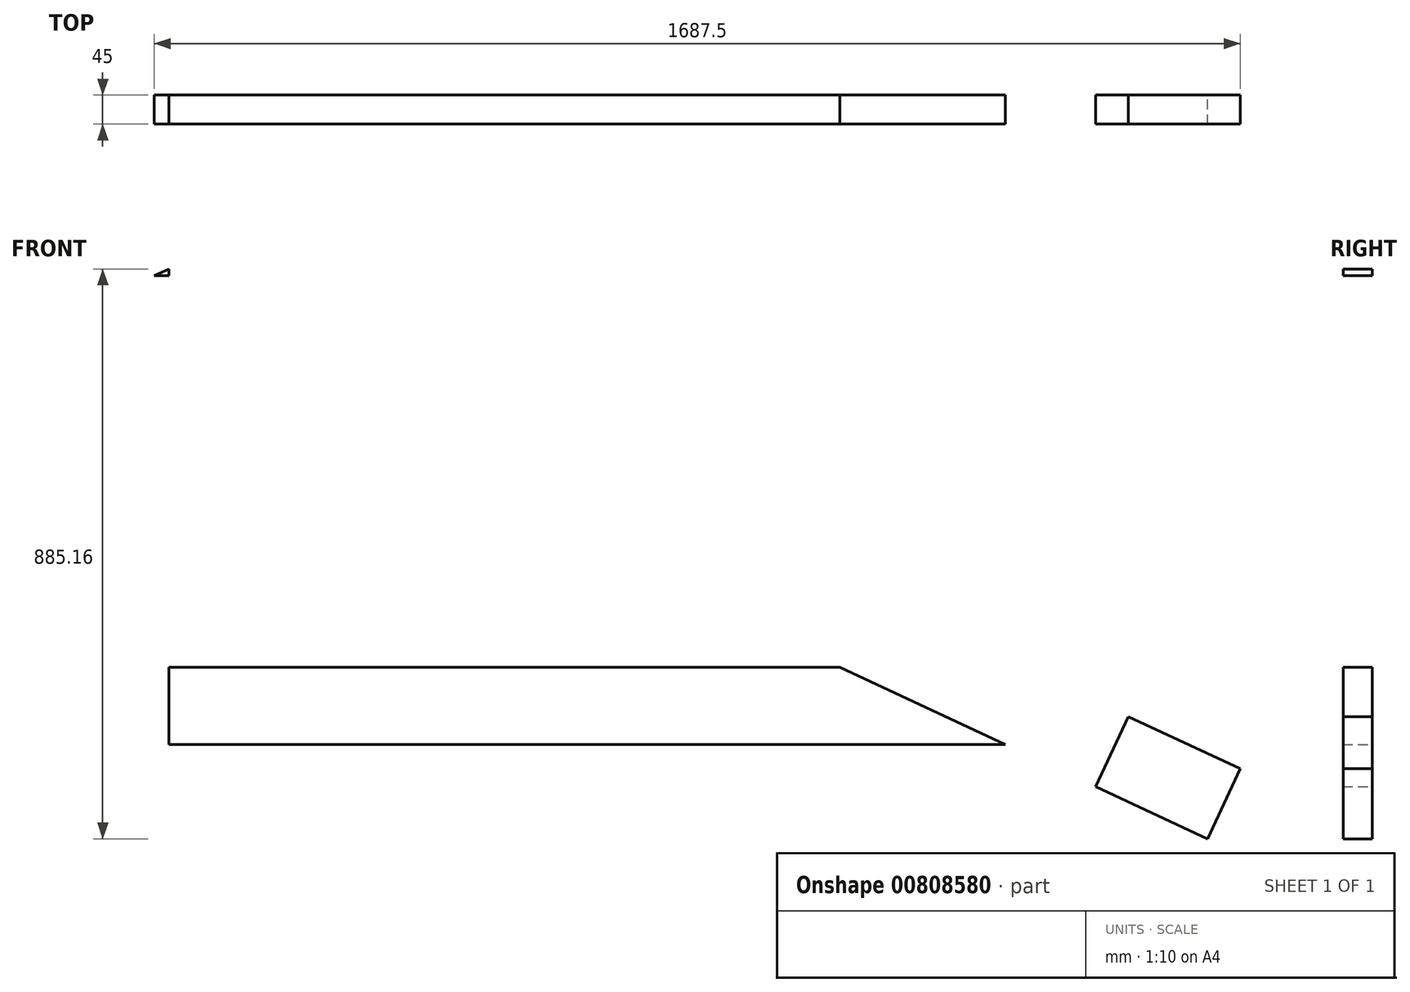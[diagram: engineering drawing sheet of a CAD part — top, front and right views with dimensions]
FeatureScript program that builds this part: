
annotation { "Feature Type Name" : "Feature", "Feature Type Description" : "" }
export const myFeature = defineFeature(function(context is Context, id is Id, definition is map)
    precondition{}
    {
        {
            var Q0;
            Q0=qCreatedBy(makeId("Front.planeOp"),FACE);
            var sketch = newSketch(context, id + "F0", { "sketchPlane" : qUnion([Q0])});
            skLineSegment(sketch, "E0", {"start": v(1614.29, 0) * mm, "end": v(0, 752.75) * mm});
            skLineSegment(sketch, "E1", {"start": v(0, 146.55) * mm, "end": v(1300, 146.55) * mm});
            skLineSegment(sketch, "E2", {"start": v(0, 885.16) * mm, "end": v(1665, 108.76) * mm});
            skLineSegment(sketch, "E3", {"start": v(1665, 108.76) * mm, "end": v(1614.29, 0) * mm});
            skLineSegment(sketch, "E4", {"start": v(0, 752.75) * mm, "end": v(-1614.29, 0) * mm});
            skLineSegment(sketch, "E5", {"start": v(0, 885.16) * mm, "end": v(-1665, 108.76) * mm});
            skLineSegment(sketch, "E6", {"start": v(-1665, 108.76) * mm, "end": v(-1614.29, 0) * mm});
            skLineSegment(sketch, "E7", {"start": v(0, 146.55) * mm, "end": v(-1300, 146.55) * mm});
            skLineSegment(sketch, "E8", {"start": v(1300, 146.55) * mm, "end": v(1300, 1.55) * mm});
            skLineSegment(sketch, "E9", {"start": v(1300, 1.55) * mm, "end": v(1210, 1.55) * mm});
            skLineSegment(sketch, "E10", {"start": v(1210, 1.55) * mm, "end": v(1210, 146.55) * mm});
            skLineSegment(sketch, "E11", {"start": v(-1042.66, 266.55) * mm, "end": v(1042.66, 266.55) * mm});
            skLineSegment(sketch, "E12", {"start": v(0, 146.55) * mm, "end": v(0, 885.16) * mm});
            skLineSegment(sketch, "E13", {"start": v(-1300, 146.55) * mm, "end": v(-1300, 1.55) * mm});
            skLineSegment(sketch, "E14", {"start": v(-1300, 1.55) * mm, "end": v(-1210, 1.55) * mm});
            skLineSegment(sketch, "E15", {"start": v(-1210, 1.55) * mm, "end": v(-1210, 146.55) * mm});
            skLineSegment(sketch, "E16", {"start": v(1614.29, 0) * mm, "end": v(1300, 0) * mm});
            skLineSegment(sketch, "E17", {"start": v(-1614.29, 0) * mm, "end": v(-1300, 0) * mm});
            skLineSegment(sketch, "E18", {"start": v(0, 885.16) * mm, "end": v(10.57, 907.82) * mm});
            skLineSegment(sketch, "E19", {"start": v(45.9, 891.34) * mm, "end": v(62.05, 925.66) * mm});
            skLineSegment(sketch, "E20", {"start": v(62.05, 925.66) * mm, "end": v(128.24, 894.87) * mm});
            skLineSegment(sketch, "E21", {"start": v(128.24, 894.87) * mm, "end": v(112.22, 860.42) * mm});
            skLineSegment(sketch, "E22", {"start": v(378.14, 735.02) * mm, "end": v(394.16, 769.47) * mm});
            skLineSegment(sketch, "E23", {"start": v(394.16, 769.47) * mm, "end": v(460.35, 738.69) * mm});
            skLineSegment(sketch, "E24", {"start": v(460.35, 738.69) * mm, "end": v(444.33, 704.23) * mm});
            skLineSegment(sketch, "E25", {"start": v(710.33, 578.61) * mm, "end": v(726.2, 613.14) * mm});
            skLineSegment(sketch, "E26", {"start": v(726.2, 613.14) * mm, "end": v(792.4, 582.35) * mm});
            skLineSegment(sketch, "E27", {"start": v(792.4, 582.35) * mm, "end": v(776.37, 547.9) * mm});
            skLineSegment(sketch, "E28", {"start": v(1043.87, 425.98) * mm, "end": v(1059.93, 460.42) * mm});
            skLineSegment(sketch, "E29", {"start": v(1059.93, 460.42) * mm, "end": v(1126.12, 429.63) * mm});
            skLineSegment(sketch, "E30", {"start": v(1126.12, 429.63) * mm, "end": v(1110.1, 395.18) * mm});
            skLineSegment(sketch, "E31", {"start": v(1376.45, 270.81) * mm, "end": v(1392.51, 305.25) * mm});
            skLineSegment(sketch, "E32", {"start": v(1392.51, 305.25) * mm, "end": v(1458.7, 274.47) * mm});
            skLineSegment(sketch, "E33", {"start": v(1458.7, 274.47) * mm, "end": v(1442.68, 240.01) * mm});
            skLineSegment(sketch, "E34", {"start": v(1364.07, 314.8) * mm, "end": v(1376.8, 352.72) * mm});
            skLineSegment(sketch, "E35", {"start": v(1762.27, 181.23) * mm, "end": v(1774.99, 219.15) * mm});
            skLineSegment(sketch, "E36", {"start": v(1376.8, 352.72) * mm, "end": v(1774.99, 219.15) * mm});
            skLineSegment(sketch, "E37", {"start": v(1364.07, 314.8) * mm, "end": v(1762.27, 181.23) * mm});
            skLineSegment(sketch, "E38", {"start": v(-22.5, 874.67) * mm, "end": v(22.5, 874.67) * mm});
            skLineSegment(sketch, "E39", {"start": v(22.5, 874.67) * mm, "end": v(22.5, 1039.67) * mm});
            skLineSegment(sketch, "E40", {"start": v(22.5, 1039.67) * mm, "end": v(-22.5, 1039.67) * mm});
            skLineSegment(sketch, "E41", {"start": v(-22.5, 1039.67) * mm, "end": v(-22.5, 874.67) * mm});
            skLineSegment(sketch, "E42", {"start": v(1031.09, 468.68) * mm, "end": v(1429.28, 335.11) * mm});
            skLineSegment(sketch, "E43", {"start": v(1429.28, 335.11) * mm, "end": v(1442, 373.03) * mm});
            skLineSegment(sketch, "E44", {"start": v(1442, 373.03) * mm, "end": v(1043.8, 506.6) * mm});
            skLineSegment(sketch, "E45", {"start": v(1043.8, 506.6) * mm, "end": v(1031.09, 468.68) * mm});
            skLineSegment(sketch, "E46", {"start": v(1721.06, 158.95) * mm, "end": v(1861.06, 158.95) * mm});
            skArc(sketch, "E47", {"start": v(1721.06, 158.95) * mm, "mid": v(1791.06, 88.95) * mm, "end": v(1861.06, 158.95) * mm});
            skLineSegment(sketch, "E48", {"start": v(1689.9, 103.02) * mm, "end": v(1712.57, 92.45) * mm});
            skLineSegment(sketch, "E49", {"start": v(1712.57, 92.45) * mm, "end": v(1659.74, -20.84) * mm});
            skLineSegment(sketch, "E50", {"start": v(1659.74, -20.84) * mm, "end": v(1637.08, -10.27) * mm});
            skLineSegment(sketch, "E51", {"start": v(1637.08, -10.27) * mm, "end": v(1689.9, 103.02) * mm});
            skLineSegment(sketch, "E52", {"start": v(1300, -10) * mm, "end": v(1628.29, -10) * mm});
            skLineSegment(sketch, "E53", {"start": v(1628.29, -10) * mm, "end": v(1628.29, 0) * mm});
            skLineSegment(sketch, "E54", {"start": v(1628.29, 0) * mm, "end": v(1300, 0) * mm});
            skLineSegment(sketch, "E55", {"start": v(1300, 1.55) * mm, "end": v(1300, -2128.45) * mm});
            skLineSegment(sketch, "E56", {"start": v(1300, -2128.45) * mm, "end": v(1203, -2128.45) * mm});
            skLineSegment(sketch, "E57", {"start": v(1203, -2128.45) * mm, "end": v(1203, 1.55) * mm});
            skLineSegment(sketch, "E58", {"start": v(1203, 1.55) * mm, "end": v(1300, 1.55) * mm});
            skLineSegment(sketch, "E59", {"start": v(-1300, 1.55) * mm, "end": v(-1300, -2128.45) * mm});
            skLineSegment(sketch, "E60", {"start": v(-1300, -2128.45) * mm, "end": v(-1203, -2128.45) * mm});
            skLineSegment(sketch, "E61", {"start": v(-1203, -2128.45) * mm, "end": v(-1203, 1.55) * mm});
            skLineSegment(sketch, "E62", {"start": v(-1203, 1.55) * mm, "end": v(-1300, 1.55) * mm});
            skLineSegment(sketch, "E63", {"start": v(-1203, 1.55) * mm, "end": v(1210, 1.55) * mm});
            skLineSegment(sketch, "E64", {"start": v(-1203, -2128.45) * mm, "end": v(1203, -2128.45) * mm});
            skLineSegment(sketch, "E65.bottom", {"start": v(-603, -198.45) * mm, "end": v(575, -198.45) * mm});
            skLineSegment(sketch, "E65.top", {"start": v(-603, -896.45) * mm, "end": v(575, -896.45) * mm});
            skLineSegment(sketch, "E65.left", {"start": v(-603, -198.45) * mm, "end": v(-603, -896.45) * mm});
            skLineSegment(sketch, "E65.right", {"start": v(575, -198.45) * mm, "end": v(575, -896.45) * mm});
            skLineSegment(sketch, "E66", {"start": v(10.57, 907.82) * mm, "end": v(1442.68, 240.01) * mm});
            skLineSegment(sketch, "E67", {"start": v(1442.68, 240.01) * mm, "end": v(1432.11, 217.35) * mm});
            skLineSegment(sketch, "E68", {"start": v(1691.06, 176.38) * mm, "end": v(1432.11, 217.35) * mm});
            skLineSegment(sketch, "E69", {"start": v(1691.06, 176.38) * mm, "end": v(1695.75, 206.01) * mm});
            skLineSegment(sketch, "E70", {"start": v(1695.75, 206.01) * mm, "end": v(1671.05, 209.92) * mm});
            skLineSegment(sketch, "E71", {"start": v(1671.05, 209.92) * mm, "end": v(1666.36, 180.29) * mm});
            skLineSegment(sketch, "E72", {"start": v(1691.06, 176.38) * mm, "end": v(1688.24, 158.6) * mm});
            skLineSegment(sketch, "E73", {"start": v(1688.24, 158.6) * mm, "end": v(1391.93, 205.49) * mm});
            skLineSegment(sketch, "E74", {"start": v(1391.93, 205.49) * mm, "end": v(1394.74, 223.27) * mm});
            skLineSegment(sketch, "E75", {"start": v(1394.74, 223.27) * mm, "end": v(1432.11, 217.35) * mm});
            skLineSegment(sketch, "E76", {"start": v(1665, 108.76) * mm, "end": v(1688.24, 158.6) * mm});
            skLineSegment(sketch, "E77", {"start": v(1630.56, 124.82) * mm, "end": v(1649.2, 164.78) * mm});
            skLineSegment(sketch, "E78", {"start": v(1688.24, 158.6) * mm, "end": v(1710.9, 148.04) * mm});
            skLineSegment(sketch, "E79", {"start": v(1710.9, 148.04) * mm, "end": v(1658.07, 34.75) * mm});
            skLineSegment(sketch, "E80", {"start": v(1658.07, 34.75) * mm, "end": v(1635.42, 45.32) * mm});
            skLineSegment(sketch, "E81", {"start": v(1721.06, 158.95) * mm, "end": v(1764.06, 158.95) * mm});
            skLineSegment(sketch, "E82", {"start": v(1095.96, 489.1) * mm, "end": v(697.76, 622.68) * mm});
            skLineSegment(sketch, "E83", {"start": v(697.76, 622.68) * mm, "end": v(710.48, 660.6) * mm});
            skLineSegment(sketch, "E84", {"start": v(710.48, 660.6) * mm, "end": v(1108.68, 527.03) * mm});
            skLineSegment(sketch, "E85", {"start": v(1108.68, 527.03) * mm, "end": v(1095.96, 489.1) * mm});
            skLineSegment(sketch, "E86", {"start": v(762.82, 643.05) * mm, "end": v(365.79, 779.2) * mm});
            skLineSegment(sketch, "E87", {"start": v(365.79, 779.2) * mm, "end": v(378.5, 817.13) * mm});
            skLineSegment(sketch, "E88", {"start": v(762.82, 643.05) * mm, "end": v(775.8, 680.88) * mm});
            skLineSegment(sketch, "E89", {"start": v(775.8, 680.88) * mm, "end": v(378.5, 817.13) * mm});
            skLineSegment(sketch, "E90", {"start": v(430.96, 799.14) * mm, "end": v(33.68, 935.39) * mm});
            skLineSegment(sketch, "E91", {"start": v(33.68, 935.39) * mm, "end": v(46.65, 973.23) * mm});
            skLineSegment(sketch, "E92", {"start": v(430.96, 799.14) * mm, "end": v(443.94, 836.98) * mm});
            skLineSegment(sketch, "E93", {"start": v(443.94, 836.98) * mm, "end": v(46.65, 973.23) * mm});
            skLineSegment(sketch, "E94", {"start": v(0, 885.16) * mm, "end": v(0, 1039.67) * mm});
            skLineSegment(sketch, "E95", {"start": v(116, 949.44) * mm, "end": v(0, 949.44) * mm});
            skCircle(sketch, "E96", {"center": v(0, 949.44) * mm, "radius": 116 * mm});
            skCircle(sketch, "E97", {"center": v(0, 949.44) * mm, "radius": 96 * mm});
            skLineSegment(sketch, "E98", {"start": v(1491.27, 189.77) * mm, "end": v(1440.55, 81.01) * mm});
            skSolve(sketch);
        }
        {
            var Q0;
            {var subQ6=sQuery(id+"F0.wireOp",EDGE,"E5");Q0=makeQuery(id+"F0.imprint","IMPRINT",FACE,{"disambiguationData":[TD([[makeQuery(id+"F0.imprint","IMPRINT",EDGE,{"derivedFrom":subQ6}),1.0]])]});}
            var Q1;
            {var subQ6=sQuery(id+"F0.wireOp",EDGE,"E2");Q1=makeQuery(id+"F0.imprint","IMPRINT",FACE,{"disambiguationData":[TD([[makeQuery(id+"F0.imprint","IMPRINT",EDGE,{"derivedFrom":subQ6}),-1.0]])]});}
            var Q2;
            {var subQ0=sQuery(id+"F0.wireOp",EDGE,"E1");Q2=makeQuery(id+"F0.imprint","IMPRINT",FACE,{"disambiguationData":[TD([[makeQuery(id+"F0.imprint","IMPRINT",EDGE,{"derivedFrom":subQ0}),1.0]])]});}
            var Q3;
            {var subQ2=sQuery(id+"F0.wireOp",EDGE,"6FhSm1Th-5a2t-2mQ5-30hT-Dnu6x7WT19CB");Q3=makeQuery(id+"F0.imprint","IMPRINT",FACE,{"disambiguationData":[TD([[makeQuery(id+"F0.imprint","IMPRINT",EDGE,{"derivedFrom":subQ2}),1.0]])]});}
            extrude(context, id + "F1", {"entities" : qUnion([Q0, Q1, Q2, Q3]), "depth" : 45 * mm, "offsetDistance" : 25 * mm});
        }
    });
